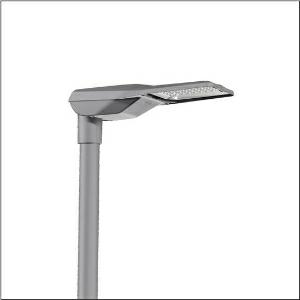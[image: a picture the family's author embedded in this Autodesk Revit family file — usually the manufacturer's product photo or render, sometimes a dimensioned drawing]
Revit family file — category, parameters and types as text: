
# Revit family: streetlight_sl_21_iq_mini___st1_0a_5xe2d31d08hb_45ae
name_source: partatom
category: Lighting Fixtures
units: mm (PartAtom-declared; Revit-internal decimal feet)

## family parameters
Cut with Voids When Loaded = No
Host = Face
Light Source = No
Part Type = Normal
Room Calculation Point = No
Round Connector Dimension = Use Diameter
Shared = No

## types (1)
- --- (1 x LED, 9450 lm, 70.9 W, 3000K)
    Apparent Load = 71 VA
    CIE Flux Codes = 37 72 97 100 100
    Color Rendering = 70
    Color Temperature = 3000K
    Default Elevation = 1800 mm
    Description = Streetlight SL 21 mini, mast luminaire, primary light control with lens, of PMMA, primary optical cover: cover, of toughened safety glass, transparent, light distribution: ST1.0a, light emission: direct distribution, primary light characteristic: asymmetric, installation type: post-top, side-entry, LED, High Power LED, rated luminous flux: 9.450lm, luminous efficacy: 133lm/W, light colour: 730, colour temperature: 3000K, control gear: ECG iQ, control: Auto-Match, Temp-Guard, Lumen-Switch, Night-Set, Smart-Wire, Light-Fading, Desk-Remote (wireless, voltage-free reading and setting of iQ features in the workshop via application-optimized NFC function/RFID function), optimised constant luminous flux control (CLO 2.0), mains connection: 220..240V, AC, 50/60Hz, start of lifetime: 71W, end of lifetime: 75W, reduction: 31W, luminaire housing, of diecast aluminium, powder-coated, Siteco® metallic grey (DB 702S), corrosivity category C5 according to DIN EN ISO 12944, length: 628mm, width: 235mm, height: 110mm, spigot size: 60/76mm (post-top) and 42/60/76mm (side-entry), mast flange for spigot size: 42mm: 5XC10008XM4, 60mm: 5XC10008XM2, 76/60mm: 5XC10108XM1, protection rating (complete): IP66, insulation class (complete): insulation class II (safety insulation), certification: CE, ENEC, VDE, impact resistance: IK09, permissible operating ambient temperature for outdoor applications: -40..+50°C, standard-compliant lighting for roads and squares, packaging unit: 1 piece

Light Distribution: ST1.0a
    Height = 110 mm
    Lamp = 1 x LED
    Lamp Light Flux = 9450 lm
    Lamp Power = 70.9 W
    Lamp count = 1
    Length = 625 mm
    Luminous efficacy = 133 lm/W
    Manufacturer = Siteco
    ModVariant = No
    Model = 5XE2D31D08HB
    Number of Poles = 1
    OnlyDefault = Yes
    Power Factor = 1
    Product Name = Streetlight SL 21 iQ mini | ST1.0a
    Product group = mast luminaire | pylon top
    ProductGroupID = 6100
    Protection Class = Protection class II
    Protection Degree = IP 66
    RLX_Detail_Level = 1
    RlxData = <blob elided: 91817 chars, md5=4467b034>
    Socket = socket
    Standby Power = 0 W
    System Light Flux = 9450 lm
    System Power = 71 W
    Type Comments = factory setting: luminous flux: 100 % | dim-lin: 254 | 711 mA
    Type Image = l_1003519.jpg
    URL = http://relux.com
    VarID = @adj_069417
    Voltage = 0 V
    Weight = 0.00 kg
    Width = 234 mm

## geometry (parser evidence)
native form markers: Blend x4, Sweep x12
no freeform markers — native parametric forms only
